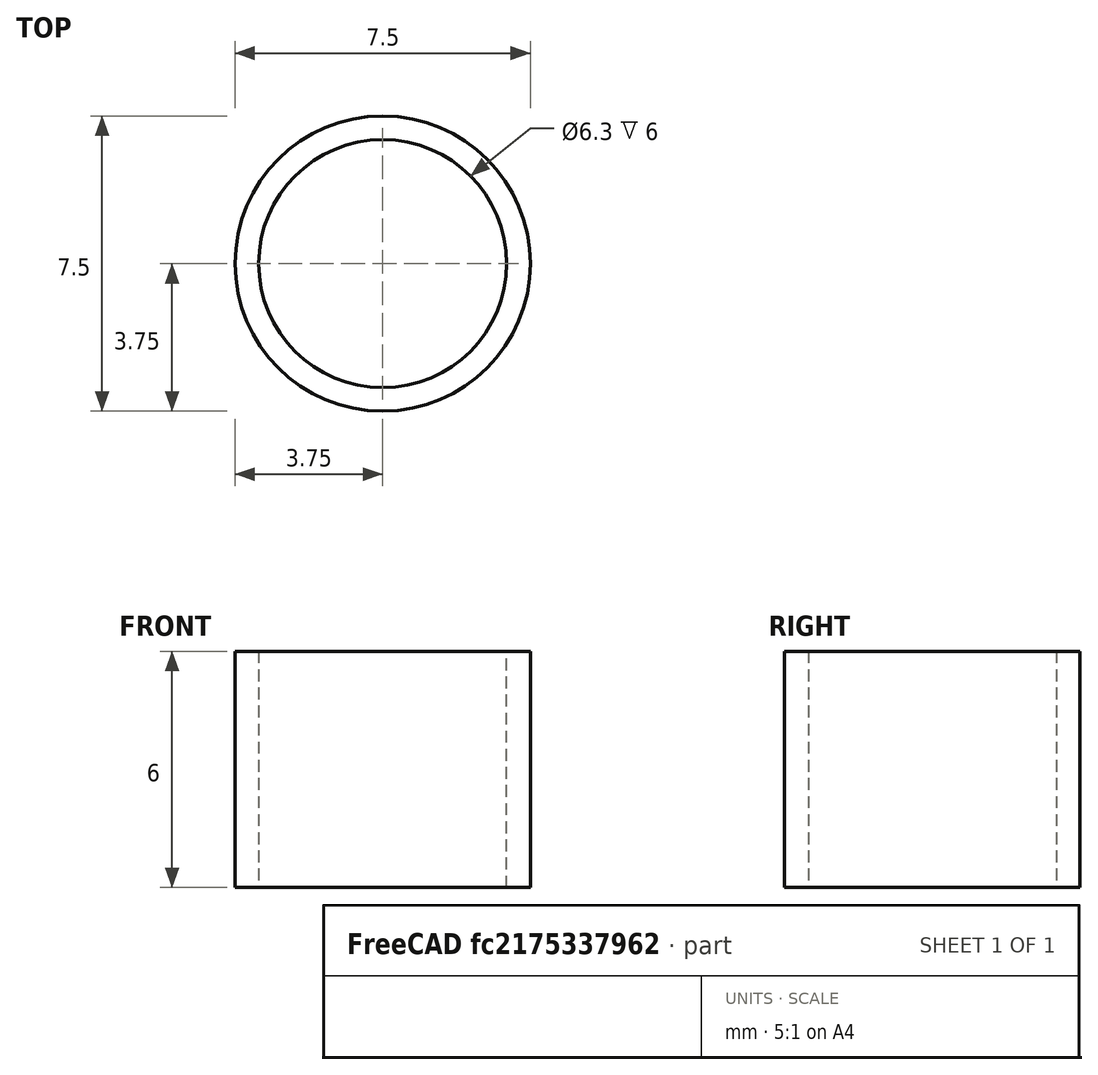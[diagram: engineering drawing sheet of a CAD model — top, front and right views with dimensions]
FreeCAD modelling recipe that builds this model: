
FCSTD DOCUMENT  (FreeCAD 0.21R33668 +26 (Git))
Label: cover_wheel
License: All rights reserved
LicenseURL: https://en.wikipedia.org/wiki/All_rights_reserved
objects: Sketcher::SketchObject×1, PartDesign::Pad×1, PartDesign::Body×1
note: 4 computed .brp shape members not serialized (recipe doc carries the construction recipe); baked Part::Feature solids carry a one-line shape summary decoded from their .brp

FEATURE [Sketcher::SketchObject] Sketch
  FullyConstrained = true
  MapMode = 5
  Support = -> [XY_Plane]
  sketch-geometry (2):
    g0: Circle CenterX=0 CenterY=0 CenterZ=0 NormalX=0 NormalY=0 NormalZ=1 AngleXU=0 Radius=3.75
    g1: Circle CenterX=0 CenterY=0 CenterZ=0 NormalX=0 NormalY=0 NormalZ=1 AngleXU=0 Radius=3.15
  constraints (4):
    c: Coincident(g0,g-1)
    c: Diameter(g0) = 7.5
    c: Coincident(g1,g0)
    c: Diameter(g1) = 6.3
FEATURE [PartDesign::Pad] Pad
  Direction = (0,0,1)
  Length = 6
  Length2 = 10
  Profile = -> Sketch
  ReferenceAxis = -> Sketch [N_Axis]
  Type = 0
FEATURE [PartDesign::Body] Body
  Group = -> [Sketch,Pad]
  Origin = -> Origin
  Tip = -> Pad
